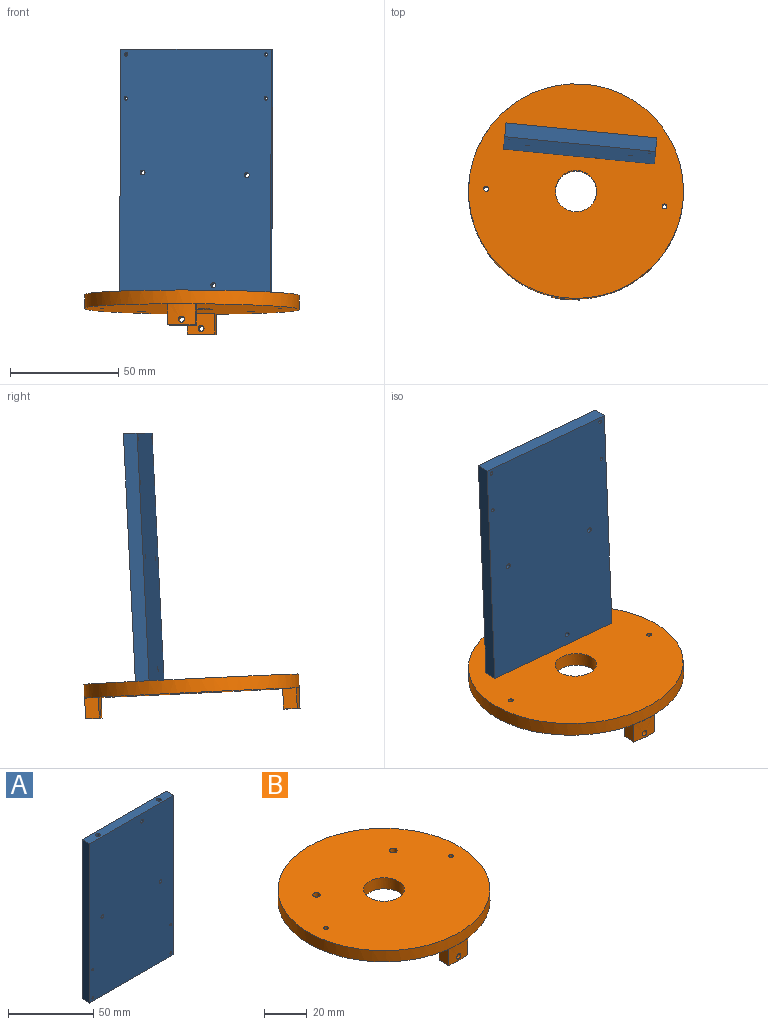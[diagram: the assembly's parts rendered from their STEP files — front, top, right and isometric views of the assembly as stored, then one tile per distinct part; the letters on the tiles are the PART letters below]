
ASSEMBLY  parts=2 mates=1
PART A: 17 faces, bbox 69.9x6.4x114.3 mm
  f0: plane 114.3x6.35mm, normal (-1,0,0), area 725.8mm2, adj f1,f3,f4,f5
  f1: plane 69.85x6.35mm, normal (0,0,-1), area 443.5mm2, adj f0,f2,f4,f5
  f2: plane 114.3x6.35mm, normal (1,0,0), area 725.8mm2, adj f1,f3,f4,f5
  f3: plane 69.85x6.35mm, normal (0,0,1), area 431.5mm2, adj f0,f2,f4,f5,f11,f13
  f4: plane 114.3x69.85mm, normal (0,-1,0), area 7963.8mm2, adj f0,f1,f2,f3,f6,f7,f8,f9
  f5: plane 114.3x69.85mm, normal (0,1,0), area 7963.8mm2, adj f0,f1,f2,f3,f6,f7,f8,f9
  f6: cylinder r=1.13mm len=6.35mm, axis (0,1,0), area 45.1mm2, adj f4,f5
  f7: cylinder r=1.13mm len=6.35mm, axis (0,1,0), area 45.1mm2, adj f4,f5
  f8: cylinder r=1.13mm len=6.35mm, axis (0,1,0), area 45.1mm2, adj f4,f5
  f9: cylinder r=0.8mm len=6.35mm, axis (0,1,0), area 31.9mm2, adj f4,f5
  f10: cylinder r=0.8mm len=6.35mm, axis (0,1,0), area 31.9mm2, adj f4,f5
  f11: cylinder r=1.38mm len=12.7mm, axis (0,0,1), area 110.5mm2, adj f3,f12
  f12: cone r=0mm half-angle=59deg, axis (0,0,1), area 7mm2, adj f11
  f13: cylinder r=1.38mm len=12.7mm, axis (0,0,1), area 110.5mm2, adj f3,f14
  f14: cone r=0mm half-angle=59deg, axis (0,0,1), area 7mm2, adj f13
  f15: cylinder r=0.8mm len=6.35mm, axis (0,1,0), area 31.9mm2, adj f4,f5
  f16: cylinder r=0.8mm len=6.35mm, axis (0,1,0), area 31.9mm2, adj f4,f5
PART B: 20 faces, bbox 99.1x99.1x15.9 mm
  f0: cylinder r=49.49mm len=12.7mm, axis (0,0,1), area 115.3mm2, adj f2,f14,f16,f17,f19
  f1: cylinder r=49.49mm len=12.7mm, axis (0,0,1), area 115.3mm2, adj f2,f10,f11,f13,f18
  f2: plane 99.06x99.06mm, normal (0,0,-1), area 7225.9mm2, adj f0,f1,f3,f5,f6,f7,f8,f9
  f3: cylinder r=49.53mm len=99.06mm, axis (0,0,-1), area 1976.2mm2, adj f2,f4
  f4: plane 99.06x99.06mm, normal (0,0,1), area 7394.1mm2, adj f3,f5,f6,f7,f8,f9
  f5: cylinder r=1.13mm len=6.35mm, axis (0,0,-1), area 45.1mm2, adj f2,f4
  f6: cylinder r=1.13mm len=6.35mm, axis (0,0,-1), area 45.1mm2, adj f2,f4
  f7: cylinder r=1.78mm len=6.35mm, axis (0,0,-1), area 70.9mm2, adj f2,f4
  f8: cylinder r=1.78mm len=6.35mm, axis (0,0,-1), area 70.9mm2, adj f2,f4
  f9: cylinder r=9.53mm len=19.05mm, axis (0,0,-1), area 380mm2, adj f2,f4
  f10: plane 9.53x6.35mm, normal (1,0,0), area 60.5mm2, adj f1,f2,f12,f13
  f11: plane 9.53x6.35mm, normal (-1,0,0), area 60.5mm2, adj f1,f2,f12,f13
  f12: plane 12.7x9.53mm, normal (0,-1,0), area 114.9mm2, adj f2,f10,f11,f13,f18
  f13: plane 12.7x6.76mm, normal (0,0,-1), area 84.1mm2, adj f1,f10,f11,f12
  f14: plane 9.53x6.35mm, normal (1,0,0), area 60.5mm2, adj f0,f2,f15,f17
  f15: plane 12.7x9.53mm, normal (0,1,0), area 114.9mm2, adj f2,f14,f16,f17,f19
  f16: plane 9.53x6.35mm, normal (-1,0,0), area 60.5mm2, adj f0,f2,f15,f17
  f17: plane 12.7x6.76mm, normal (0,0,-1), area 84.1mm2, adj f0,f14,f15,f16
  f18: cylinder r=1.38mm len=6.76mm, axis (0,-1,0), area 58.7mm2, adj f1,f12
  f19: cylinder r=1.38mm len=6.76mm, axis (0,1,0), area 58.7mm2, adj f0,f15
PLACE A rot(axis=(1,-0.05,0),177.2deg) t=(-53.83,44.06,9.31)mm
PLACE B rot(axis=(-0.44,0.02,-0.9),6.3deg) t=(-55.19,27.79,3.74)mm
MATE fastened B.f8 <-> A.f13  axis (0,0.05,1) through (-27.99,44.69,9.15)mm
